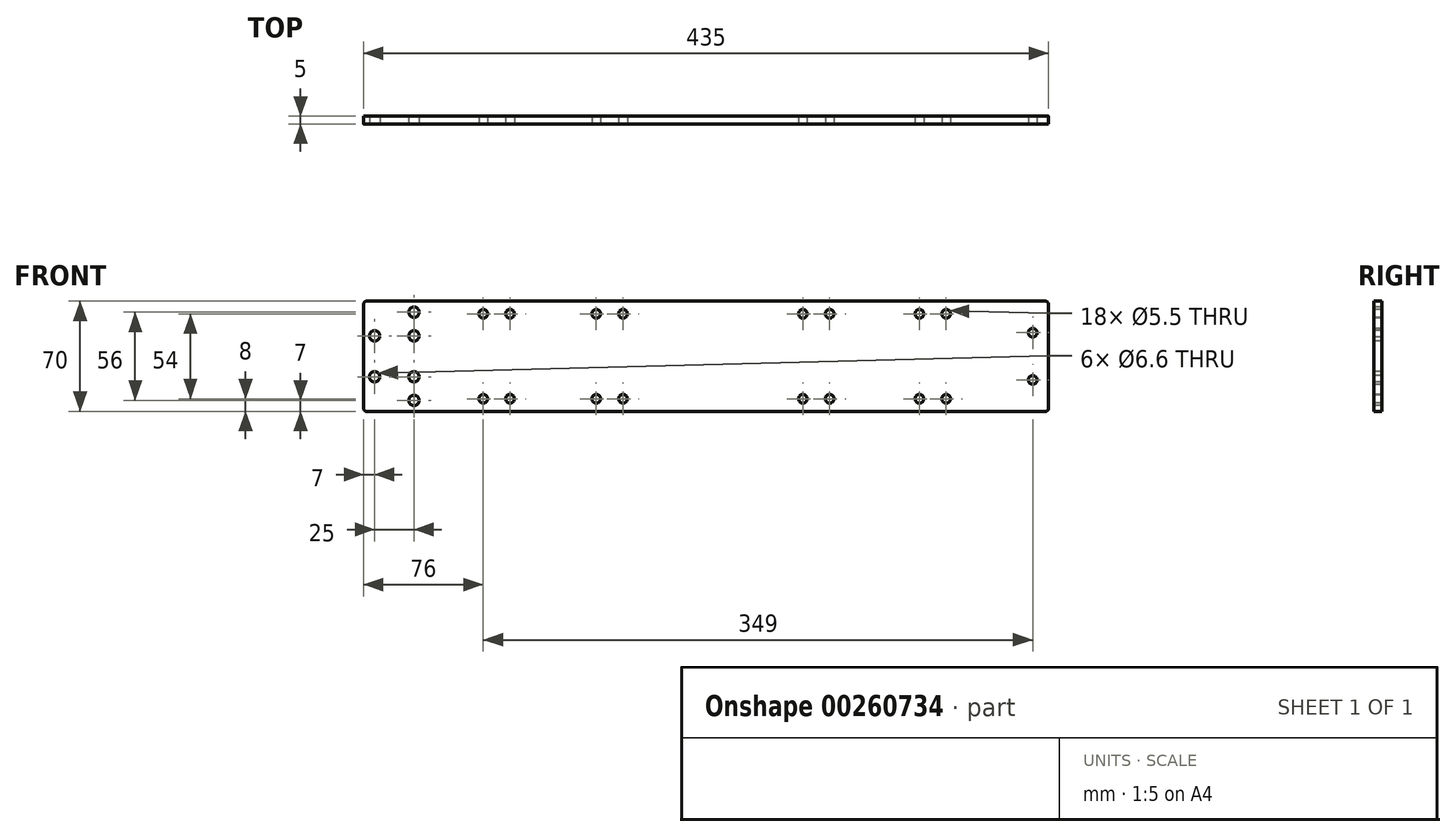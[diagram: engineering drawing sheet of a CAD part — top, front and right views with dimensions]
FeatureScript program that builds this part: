
annotation { "Feature Type Name" : "Feature", "Feature Type Description" : "" }
export const myFeature = defineFeature(function(context is Context, id is Id, definition is map)
    precondition{}
    {
        {
            var Q0;
            Q0=qCreatedBy(makeId("Front.planeOp"),FACE);
            var sketch = newSketch(context, id + "F0", { "sketchPlane" : qUnion([Q0])});
            skLineSegment(sketch, "E0.bottom", {"start": v(217.5, 35) * mm, "end": v(-217.5, 35) * mm});
            skLineSegment(sketch, "E0.top", {"start": v(217.5, -35) * mm, "end": v(-217.5, -35) * mm});
            skLineSegment(sketch, "E0.left", {"start": v(217.5, 35) * mm, "end": v(217.5, -35) * mm});
            skLineSegment(sketch, "E0.right", {"start": v(-217.5, 35) * mm, "end": v(-217.5, -35) * mm});
            skPoint(sketch, "E0.middle", {"position": v(0, 0) * mm});
            skSolve(sketch);
        }
        {
            var Q0;
            Q0=makeQuery(id+"F0.imprint","IMPRINT",FACE,{"disambiguationData":[TD([[makeQuery(id+"F0.imprint","IMPRINT",EDGE,{"derivedFrom":sQuery(id+"F0.wireOp",EDGE,"E0.bottom")}),1.0]])]});
            extrude(context, id + "F1", {"entities" : qUnion([Q0]), "depth" : 5 * mm});
        }
        {
            var Q0;
            Q0=makeQuery(id+"F1.opExtrude","SWEPT_EDGE",EDGE,{"disambiguationData":[OSD([sQuery(id+"F0.wireOp",EDGE,"E0.bottom"),sQuery(id+"F0.wireOp",EDGE,"E0.left")])]});
            var Q1;
            Q1=makeQuery(id+"F1.opExtrude","SWEPT_EDGE",EDGE,{"disambiguationData":[OSD([sQuery(id+"F0.wireOp",EDGE,"E0.top"),sQuery(id+"F0.wireOp",EDGE,"E0.left")])]});
            var Q2;
            Q2=makeQuery(id+"F1.opExtrude","SWEPT_EDGE",EDGE,{"disambiguationData":[OSD([sQuery(id+"F0.wireOp",EDGE,"E0.bottom"),sQuery(id+"F0.wireOp",EDGE,"E0.right")])]});
            var Q3;
            Q3=makeQuery(id+"F1.opExtrude","SWEPT_EDGE",EDGE,{"disambiguationData":[OSD([sQuery(id+"F0.wireOp",EDGE,"E0.top"),sQuery(id+"F0.wireOp",EDGE,"E0.right")])]});
            fillet(context, id + "F2", {"entities" : qUnion([Q0, Q1, Q2, Q3]), "radius" : 2 * mm, "tangentPropagation" : true, "allowEdgeOverflow" : false});
        }
        {
            var Q0;
            Q0=makeQuery(id+"F1.opExtrude","CAP_FACE",FACE,{"disambiguationData":[OSD([sQuery(id+"F0.wireOp",EDGE,"E0.bottom"),sQuery(id+"F0.wireOp",EDGE,"E0.top"),sQuery(id+"F0.wireOp",EDGE,"E0.left"),sQuery(id+"F0.wireOp",EDGE,"E0.right")])],"isStart":false});
            var sketch = newSketch(context, id + "F3", { "sketchPlane" : qUnion([Q0])});
            skPoint(sketch, "E1", {"position": v(-210.5, 13) * mm});
            skPoint(sketch, "E2", {"position": v(-210.5, -13) * mm});
            skPoint(sketch, "E3", {"position": v(-185.5, -13) * mm});
            skPoint(sketch, "E4", {"position": v(-185.5, 13) * mm});
            skPoint(sketch, "E5", {"position": v(-173.88, 0) * mm});
            skPoint(sketch, "E6", {"position": v(-185.5, 28) * mm});
            skPoint(sketch, "E7", {"position": v(-185.5, -28) * mm});
            skSolve(sketch);
        }
        {
            var Q0;
            Q0=sQuery(id+"F3.wireOp",VERTEX,"E4");
            var Q1;
            Q1=sQuery(id+"F3.wireOp",VERTEX,"E1");
            var Q2;
            Q2=sQuery(id+"F3.wireOp",VERTEX,"E2");
            var Q3;
            Q3=sQuery(id+"F3.wireOp",VERTEX,"E3");
            var Q4;
            Q4=sQuery(id+"F3.wireOp",VERTEX,"E6");
            var Q5;
            Q5=sQuery(id+"F3.wireOp",VERTEX,"E7");
            var Q6;
            Q6=makeQuery(id+"F1.opExtrude","SWEPT_BODY",BODY,{"disambiguationData":[OSD([sQuery(id+"F0.wireOp",EDGE,"E0.bottom"),sQuery(id+"F0.wireOp",EDGE,"E0.top"),sQuery(id+"F0.wireOp",EDGE,"E0.left"),sQuery(id+"F0.wireOp",EDGE,"E0.right")])]});
            hole(context, id + "F4", {"style" : HoleStyle.SIMPLE, "endStyle" : HoleEndStyle.THROUGH, "standardTappedOrClearance" : lookupTablePath({ "standard" : "ISO", "fit" : "Normal", "size" : "M6", "type" : "Clearance" }), "standardBlindInLast" : lookupTablePath({ "fit" : "Standard", "standard" : "ISO", "size" : "M6", "type" : "Clearance" }), "holeDiameter" : 6.6 * mm, "tappedDepth" : 12.7 * mm, "tapClearance" : 3, "locations" : qUnion([Q0, Q1, Q2, Q3, Q4, Q5]), "scope" : qUnion([Q6])});
        }
        {
            var Q0;
            Q0=makeQuery(id+"F1.opExtrude","CAP_FACE",FACE,{"disambiguationData":[OSD([sQuery(id+"F0.wireOp",EDGE,"E0.bottom"),sQuery(id+"F0.wireOp",EDGE,"E0.top"),sQuery(id+"F0.wireOp",EDGE,"E0.left"),sQuery(id+"F0.wireOp",EDGE,"E0.right")])],"isStart":false});
            var sketch = newSketch(context, id + "F5", { "sketchPlane" : qUnion([Q0])});
            skPoint(sketch, "E8", {"position": v(-124.5, 0) * mm});
            skPoint(sketch, "E9", {"position": v(-141.5, 0) * mm});
            skPoint(sketch, "E10", {"position": v(-141.5, -27) * mm});
            skPoint(sketch, "E11", {"position": v(-141.5, 27) * mm});
            skPoint(sketch, "E12", {"position": v(-124.5, 27) * mm});
            skPoint(sketch, "E13", {"position": v(-124.5, -27) * mm});
            skSolve(sketch);
        }
        {
            var Q0;
            Q0=sQuery(id+"F5.wireOp",VERTEX,"a9f0f2d9-f7fe-4d6d-92ca-6f259901119f");
            var Q1;
            Q1=sQuery(id+"F5.wireOp",VERTEX,"E11");
            var Q2;
            Q2=sQuery(id+"F5.wireOp",VERTEX,"E12");
            var Q3;
            Q3=sQuery(id+"F5.wireOp",VERTEX,"E10");
            var Q4;
            Q4=sQuery(id+"F5.wireOp",VERTEX,"E13");
            var Q5;
            Q5=makeQuery(id+"F1.opExtrude","SWEPT_BODY",BODY,{"disambiguationData":[OSD([sQuery(id+"F0.wireOp",EDGE,"E0.bottom"),sQuery(id+"F0.wireOp",EDGE,"E0.top"),sQuery(id+"F0.wireOp",EDGE,"E0.left"),sQuery(id+"F0.wireOp",EDGE,"E0.right")])]});
            hole(context, id + "F6", {"style" : HoleStyle.SIMPLE, "endStyle" : HoleEndStyle.THROUGH, "standardTappedOrClearance" : lookupTablePath({ "standard" : "ISO", "fit" : "Normal", "size" : "M5", "type" : "Clearance" }), "standardBlindInLast" : lookupTablePath({ "fit" : "Standard", "standard" : "ISO", "size" : "M5", "type" : "Clearance" }), "holeDiameter" : 5.5 * mm, "tappedDepth" : 12.7 * mm, "tapClearance" : 3, "locations" : qUnion([Q0, Q1, Q2, Q3, Q4]), "scope" : qUnion([Q5])});
        }
        {
            var Q0;
            Q0=makeQuery(id+"F1.opExtrude","CAP_FACE",FACE,{"disambiguationData":[OSD([sQuery(id+"F0.wireOp",EDGE,"E0.bottom"),sQuery(id+"F0.wireOp",EDGE,"E0.top"),sQuery(id+"F0.wireOp",EDGE,"E0.left"),sQuery(id+"F0.wireOp",EDGE,"E0.right")])],"isStart":false});
            var sketch = newSketch(context, id + "F7", { "sketchPlane" : qUnion([Q0])});
            skPoint(sketch, "E14", {"position": v(-69.75, 27) * mm});
            skPoint(sketch, "E15", {"position": v(-52.75, 27) * mm});
            skPoint(sketch, "E16", {"position": v(-69.75, -27) * mm});
            skPoint(sketch, "E17", {"position": v(-52.75, -27) * mm});
            skPoint(sketch, "E18", {"position": v(61.5, 27) * mm});
            skPoint(sketch, "E19", {"position": v(78.5, 27) * mm});
            skPoint(sketch, "E20", {"position": v(135.5, 27) * mm});
            skPoint(sketch, "E21", {"position": v(152.5, 27) * mm});
            skPoint(sketch, "E22", {"position": v(61.5, -27) * mm});
            skPoint(sketch, "E23", {"position": v(78.5, -27) * mm});
            skPoint(sketch, "E24", {"position": v(135.5, -27) * mm});
            skPoint(sketch, "E25", {"position": v(152.5, -27) * mm});
            skSolve(sketch);
        }
        {
            var Q0;
            Q0=sQuery(id+"F7.wireOp",VERTEX,"E14");
            var Q1;
            Q1=sQuery(id+"F7.wireOp",VERTEX,"E15");
            var Q2;
            Q2=sQuery(id+"F7.wireOp",VERTEX,"E16");
            var Q3;
            Q3=sQuery(id+"F7.wireOp",VERTEX,"E17");
            var Q4;
            Q4=sQuery(id+"F7.wireOp",VERTEX,"bda97d19-54d3-4f9a-ae8f-edd01fa22da7");
            var Q5;
            Q5=sQuery(id+"F7.wireOp",VERTEX,"52c89dd3-b31e-415d-a119-d1046fae07b4");
            var Q6;
            Q6=sQuery(id+"F7.wireOp",VERTEX,"f939c555-2940-45b5-bef9-441bb8b3a3d4");
            var Q7;
            Q7=sQuery(id+"F7.wireOp",VERTEX,"99c24194-43a8-4f88-898b-146b6796950a");
            var Q8;
            Q8=sQuery(id+"F7.wireOp",VERTEX,"E18");
            var Q9;
            Q9=sQuery(id+"F7.wireOp",VERTEX,"E19");
            var Q10;
            Q10=sQuery(id+"F7.wireOp",VERTEX,"E22");
            var Q11;
            Q11=sQuery(id+"F7.wireOp",VERTEX,"E23");
            var Q12;
            Q12=sQuery(id+"F7.wireOp",VERTEX,"E20");
            var Q13;
            Q13=sQuery(id+"F7.wireOp",VERTEX,"E21");
            var Q14;
            Q14=sQuery(id+"F7.wireOp",VERTEX,"E24");
            var Q15;
            Q15=sQuery(id+"F7.wireOp",VERTEX,"E25");
            var Q16;
            Q16=makeQuery(id+"F1.opExtrude","SWEPT_BODY",BODY,{"disambiguationData":[OSD([sQuery(id+"F0.wireOp",EDGE,"E0.bottom"),sQuery(id+"F0.wireOp",EDGE,"E0.top"),sQuery(id+"F0.wireOp",EDGE,"E0.left"),sQuery(id+"F0.wireOp",EDGE,"E0.right")])]});
            hole(context, id + "F8", {"style" : HoleStyle.SIMPLE, "endStyle" : HoleEndStyle.THROUGH, "standardTappedOrClearance" : lookupTablePath({ "standard" : "ISO", "fit" : "Normal", "size" : "M5", "type" : "Clearance" }), "standardBlindInLast" : lookupTablePath({ "fit" : "Standard", "standard" : "ISO", "size" : "M5", "type" : "Clearance" }), "holeDiameter" : 5.5 * mm, "tappedDepth" : 12.7 * mm, "tapClearance" : 3, "locations" : qUnion([Q0, Q1, Q2, Q3, Q4, Q5, Q6, Q7, Q8, Q9, Q10, Q11, Q12, Q13, Q14, Q15]), "scope" : qUnion([Q16])});
        }
        {
            var Q0;
            Q0=makeQuery(id+"F1.opExtrude","CAP_FACE",FACE,{"disambiguationData":[OSD([sQuery(id+"F0.wireOp",EDGE,"E0.bottom"),sQuery(id+"F0.wireOp",EDGE,"E0.top"),sQuery(id+"F0.wireOp",EDGE,"E0.left"),sQuery(id+"F0.wireOp",EDGE,"E0.right")])],"isStart":false});
            var sketch = newSketch(context, id + "F9", { "sketchPlane" : qUnion([Q0])});
            skPoint(sketch, "E26", {"position": v(207.5, 0) * mm});
            skPoint(sketch, "E27", {"position": v(207.5, 15) * mm});
            skPoint(sketch, "E28", {"position": v(207.5, -15) * mm});
            skSolve(sketch);
        }
        {
            var Q0;
            Q0=sQuery(id+"F9.wireOp",VERTEX,"E27");
            var Q1;
            Q1=sQuery(id+"F9.wireOp",VERTEX,"E28");
            var Q2;
            Q2=makeQuery(id+"F1.opExtrude","SWEPT_BODY",BODY,{"disambiguationData":[OSD([sQuery(id+"F0.wireOp",EDGE,"E0.bottom"),sQuery(id+"F0.wireOp",EDGE,"E0.top"),sQuery(id+"F0.wireOp",EDGE,"E0.left"),sQuery(id+"F0.wireOp",EDGE,"E0.right")])]});
            hole(context, id + "F10", {"style" : HoleStyle.SIMPLE, "endStyle" : HoleEndStyle.THROUGH, "standardTappedOrClearance" : lookupTablePath({ "standard" : "ISO", "fit" : "Normal", "size" : "M5", "type" : "Clearance" }), "standardBlindInLast" : lookupTablePath({ "fit" : "Standard", "standard" : "ISO", "size" : "M5", "type" : "Clearance" }), "holeDiameter" : 5.5 * mm, "tappedDepth" : 12.7 * mm, "tapClearance" : 3, "locations" : qUnion([Q0, Q1]), "scope" : qUnion([Q2])});
        }
    });
